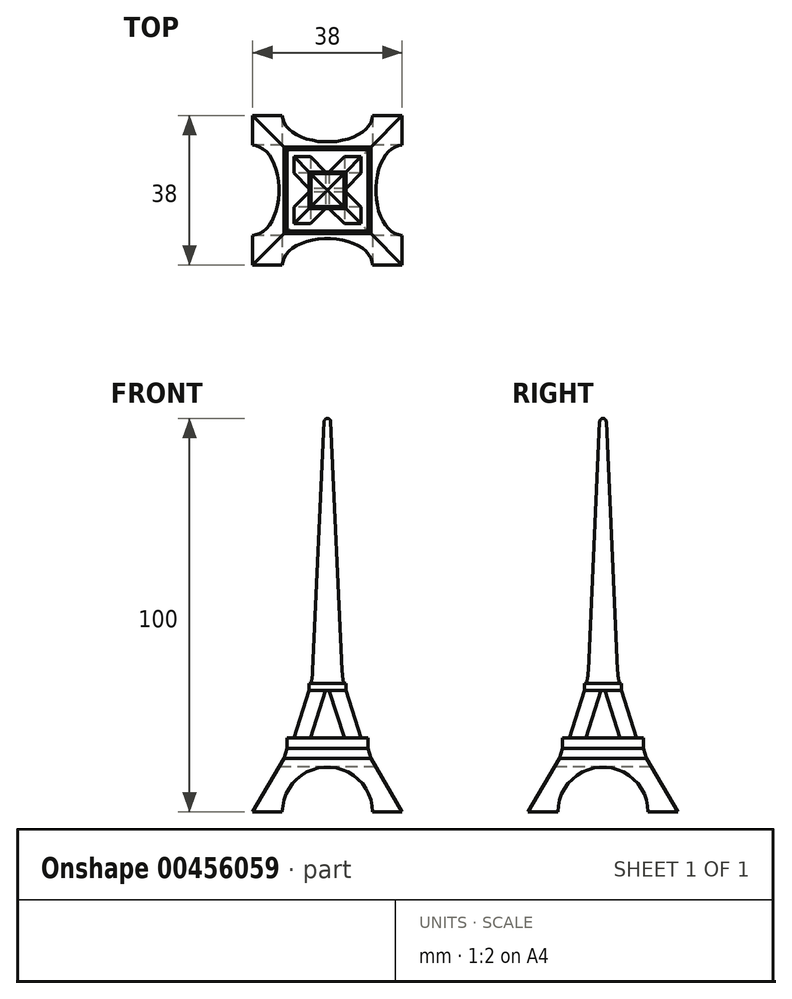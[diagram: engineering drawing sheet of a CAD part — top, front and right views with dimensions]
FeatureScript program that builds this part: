
annotation { "Feature Type Name" : "Feature", "Feature Type Description" : "" }
export const myFeature = defineFeature(function(context is Context, id is Id, definition is map)
    precondition{}
    {
        {
            var Q0;
            Q0=qCreatedBy(makeId("Front.planeOp"),FACE);
            var sketch = newSketch(context, id + "F0", { "sketchPlane" : qUnion([Q0])});
            skLineSegment(sketch, "E0.bottom", {"start": v(0, 0) * mm, "end": v(38, 0) * mm});
            skLineSegment(sketch, "E0.top", {"start": v(0, 100) * mm, "end": v(38, 100) * mm});
            skLineSegment(sketch, "E0.left", {"start": v(0, 0) * mm, "end": v(0, 100) * mm});
            skLineSegment(sketch, "E0.right", {"start": v(38, 0) * mm, "end": v(38, 100) * mm});
            skSolve(sketch);
        }
        {
            var Q0;
            Q0=makeQuery(id+"F0.imprint","IMPRINT",FACE,{"disambiguationData":[TD([[makeQuery(id+"F0.imprint","IMPRINT",EDGE,{"derivedFrom":sQuery(id+"F0.wireOp",EDGE,"E0.bottom")}),1.0]])]});
            extrude(context, id + "F1", {"entities" : qUnion([Q0]), "depth" : 38 * mm});
        }
        {
            var Q0;
            Q0=makeQuery(id+"F1.opExtrude","CAP_FACE",FACE,{"disambiguationData":[OSD([sQuery(id+"F0.wireOp",EDGE,"E0.bottom"),sQuery(id+"F0.wireOp",EDGE,"E0.top"),sQuery(id+"F0.wireOp",EDGE,"E0.left"),sQuery(id+"F0.wireOp",EDGE,"E0.right")])],"isStart":false});
            var sketch = newSketch(context, id + "F2", { "sketchPlane" : qUnion([Q0])});
            skPoint(sketch, "E1.endSnap0", {"position": v(19, 100) * mm});
            skLineSegment(sketch, "E2", {"start": v(19, 100) * mm, "end": v(19, 0) * mm, "construction": true});
            skLineSegment(sketch, "E3", {"start": v(19, 100) * mm, "end": v(19.03, 100) * mm});
            skLineSegment(sketch, "E4", {"start": v(19.83, 99.24) * mm, "end": v(22.72, 36.04) * mm});
            skLineSegment(sketch, "E5", {"start": v(38, 0) * mm, "end": v(29.32, 14.77) * mm});
            skLineSegment(sketch, "E6", {"start": v(27.53, 18.8) * mm, "end": v(23.66, 30.85) * mm});
            skArc(sketch, "E7", {"start": v(30.49, 0) * mm, "mid": v(27.12, 8.12) * mm, "end": v(19, 11.49) * mm});
            skLineSegment(sketch, "E8", {"start": v(38, 0) * mm, "end": v(30.49, 0) * mm});
            skPoint(sketch, "E9.visualSharp", {"position": v(22.85, 33.38) * mm});
            skArc(sketch, "E9.filletArc", {"start": v(22.72, 36.04) * mm, "mid": v(22.88, 34.33) * mm, "end": v(23.17, 32.64) * mm});
            skPoint(sketch, "E10.visualSharp", {"position": v(28.2, 16.68) * mm});
            skLineSegment(sketch, "E11.MirrorCS", {"start": v(18.17, 99.24) * mm, "end": v(15.28, 36.04) * mm});
            skArc(sketch, "E12.MirrorCS", {"start": v(15.28, 36.04) * mm, "mid": v(15.12, 34.33) * mm, "end": v(14.83, 32.64) * mm});
            skLineSegment(sketch, "E13.MirrorCS", {"start": v(10.47, 18.8) * mm, "end": v(14.34, 30.85) * mm});
            skLineSegment(sketch, "E14.MirrorCS", {"start": v(19, 100) * mm, "end": v(18.97, 100) * mm});
            skLineSegment(sketch, "E15.MirrorCS", {"start": v(0, 0) * mm, "end": v(8.68, 14.77) * mm});
            skArc(sketch, "E16.MirrorCS", {"start": v(7.51, 0) * mm, "mid": v(10.88, 8.12) * mm, "end": v(19, 11.49) * mm});
            skLineSegment(sketch, "E17.MirrorCS", {"start": v(0, 0) * mm, "end": v(7.51, 0) * mm});
            skLineSegment(sketch, "E18.bottom", {"start": v(-8.57, -4.89) * mm, "end": v(50.47, -4.89) * mm});
            skLineSegment(sketch, "E18.top", {"start": v(-8.57, 109.12) * mm, "end": v(50.47, 109.12) * mm});
            skLineSegment(sketch, "E18.left", {"start": v(-8.57, -4.89) * mm, "end": v(-8.57, 109.12) * mm});
            skLineSegment(sketch, "E18.right", {"start": v(50.47, -4.89) * mm, "end": v(50.47, 109.12) * mm});
            skLineSegment(sketch, "E19", {"start": v(29.32, 14.77) * mm, "end": v(29.32, 18.8) * mm});
            skLineSegment(sketch, "E20", {"start": v(29.32, 18.8) * mm, "end": v(27.53, 18.8) * mm});
            skLineSegment(sketch, "E21.MirrorCS", {"start": v(8.68, 18.8) * mm, "end": v(10.47, 18.8) * mm});
            skLineSegment(sketch, "E22.MirrorCS", {"start": v(8.68, 14.77) * mm, "end": v(8.68, 18.8) * mm});
            skLineSegment(sketch, "E23", {"start": v(23.66, 30.85) * mm, "end": v(23.66, 32.64) * mm});
            skLineSegment(sketch, "E24", {"start": v(23.66, 32.64) * mm, "end": v(23.17, 32.64) * mm});
            skLineSegment(sketch, "E25.MirrorCS", {"start": v(14.34, 30.85) * mm, "end": v(14.34, 32.64) * mm});
            skLineSegment(sketch, "E26.MirrorCS", {"start": v(14.34, 32.64) * mm, "end": v(14.83, 32.64) * mm});
            skPoint(sketch, "E27.orphan", {"position": v(14.34, 30.85) * mm});
            skPoint(sketch, "E28.visualSharp", {"position": v(18.2, 100) * mm});
            skArc(sketch, "E28.filletArc", {"start": v(18.97, 100) * mm, "mid": v(18.42, 99.78) * mm, "end": v(18.17, 99.24) * mm});
            skPoint(sketch, "E29.visualSharp", {"position": v(19.8, 100) * mm});
            skArc(sketch, "E29.filletArc", {"start": v(19.83, 99.24) * mm, "mid": v(19.58, 99.78) * mm, "end": v(19.03, 100) * mm});
            skLineSegment(sketch, "E30.0", {"start": v(14.67, 18.8) * mm, "end": v(18.54, 30.85) * mm});
            skLineSegment(sketch, "E31.0", {"start": v(23.33, 18.8) * mm, "end": v(19.46, 30.85) * mm});
            skLineSegment(sketch, "E32", {"start": v(23.33, 18.8) * mm, "end": v(14.67, 18.8) * mm});
            skLineSegment(sketch, "E33", {"start": v(19.46, 30.85) * mm, "end": v(18.54, 30.85) * mm});
            skSolve(sketch);
        }
        {
            var Q0;
            {var subQ2=sQuery(id+"F2.wireOp",EDGE,"E11.MirrorCS");Q0=makeQuery(id+"F2.imprint","IMPRINT",FACE,{"disambiguationData":[TD([[makeQuery(id+"F2.imprint","IMPRINT",EDGE,{"derivedFrom":subQ2}),-1.0]])]});}
            var Q1;
            {var subQ0=sQuery(id+"F2.wireOp",EDGE,"E7");Q1=makeQuery(id+"F2.imprint","IMPRINT",FACE,{"disambiguationData":[TD([[makeQuery(id+"F2.imprint","IMPRINT",EDGE,{"derivedFrom":subQ0}),1.0]])]});}
            var Q2;
            {var subQ2=sQuery(id+"F2.wireOp",EDGE,"E4");Q2=makeQuery(id+"F2.imprint","IMPRINT",FACE,{"disambiguationData":[TD([[makeQuery(id+"F2.imprint","IMPRINT",EDGE,{"derivedFrom":subQ2}),1.0]])]});}
            var Q3;
            Q3=makeQuery(id+"F2.imprint","IMPRINT",FACE,{"disambiguationData":[TD([[makeQuery(id+"F2.imprint","IMPRINT",EDGE,{"derivedFrom":sQuery(id+"F2.wireOp",EDGE,"E30.0")}),-1.0]])]});
            extrude(context, id + "F3", {"entities" : qUnion([Q0, Q1, Q2, Q3]), "operationType" : NewBodyOperationType.REMOVE, "endBound" : BoundingType.THROUGH_ALL, "oppositeDirection" : true, "depth" : 25 * mm});
        }
        {
            var Q0;
            Q0=qCreatedBy(makeId("Right.planeOp"),FACE);
            var sketch = newSketch(context, id + "F4", { "sketchPlane" : qUnion([Q0])});
            skPoint(sketch, "E34.endSnap0", {"position": v(-19, 100) * mm});
            skLineSegment(sketch, "E35", {"start": v(-19, 100) * mm, "end": v(-19, 0) * mm, "construction": true});
            skLineSegment(sketch, "E36", {"start": v(-19, 100) * mm, "end": v(-18.97, 100) * mm});
            skLineSegment(sketch, "E37", {"start": v(-18.17, 99.24) * mm, "end": v(-15.28, 36.04) * mm});
            skLineSegment(sketch, "E38", {"start": v(0, 0) * mm, "end": v(-8.68, 14.77) * mm});
            skLineSegment(sketch, "E39", {"start": v(-10.47, 18.8) * mm, "end": v(-14.34, 30.85) * mm});
            skArc(sketch, "E40", {"start": v(-7.51, 0) * mm, "mid": v(-10.88, 8.12) * mm, "end": v(-19, 11.49) * mm});
            skLineSegment(sketch, "E41", {"start": v(0, 0) * mm, "end": v(-7.51, 0) * mm});
            skPoint(sketch, "E42.visualSharp", {"position": v(-15.15, 33.38) * mm});
            skArc(sketch, "E42.filletArc", {"start": v(-15.28, 36.04) * mm, "mid": v(-15.12, 34.33) * mm, "end": v(-14.83, 32.64) * mm});
            skPoint(sketch, "E43.visualSharp", {"position": v(-9.8, 16.68) * mm});
            skLineSegment(sketch, "E44.MirrorCS", {"start": v(-19.83, 99.24) * mm, "end": v(-22.72, 36.04) * mm});
            skArc(sketch, "E45.MirrorCS", {"start": v(-22.72, 36.04) * mm, "mid": v(-22.88, 34.33) * mm, "end": v(-23.17, 32.64) * mm});
            skLineSegment(sketch, "E46.MirrorCS", {"start": v(-27.53, 18.8) * mm, "end": v(-23.66, 30.85) * mm});
            skLineSegment(sketch, "E47.MirrorCS", {"start": v(-19, 100) * mm, "end": v(-19.03, 100) * mm});
            skLineSegment(sketch, "E48.MirrorCS", {"start": v(-38, 0) * mm, "end": v(-29.32, 14.77) * mm});
            skArc(sketch, "E49.MirrorCS", {"start": v(-30.49, 0) * mm, "mid": v(-27.12, 8.12) * mm, "end": v(-19, 11.49) * mm});
            skLineSegment(sketch, "E50.MirrorCS", {"start": v(-38, 0) * mm, "end": v(-30.49, 0) * mm});
            skLineSegment(sketch, "E51.bottom", {"start": v(-46.57, -4.89) * mm, "end": v(12.47, -4.89) * mm});
            skLineSegment(sketch, "E51.top", {"start": v(-46.57, 109.12) * mm, "end": v(12.47, 109.12) * mm});
            skLineSegment(sketch, "E51.left", {"start": v(-46.57, -4.89) * mm, "end": v(-46.57, 109.12) * mm});
            skLineSegment(sketch, "E51.right", {"start": v(12.47, -4.89) * mm, "end": v(12.47, 109.12) * mm});
            skLineSegment(sketch, "E52", {"start": v(-8.68, 14.77) * mm, "end": v(-8.68, 18.8) * mm});
            skLineSegment(sketch, "E53", {"start": v(-8.68, 18.8) * mm, "end": v(-10.47, 18.8) * mm});
            skLineSegment(sketch, "E54.MirrorCS", {"start": v(-29.32, 18.8) * mm, "end": v(-27.53, 18.8) * mm});
            skLineSegment(sketch, "E55.MirrorCS", {"start": v(-29.32, 14.77) * mm, "end": v(-29.32, 18.8) * mm});
            skLineSegment(sketch, "E56", {"start": v(-14.34, 30.85) * mm, "end": v(-14.34, 32.64) * mm});
            skLineSegment(sketch, "E57", {"start": v(-14.34, 32.64) * mm, "end": v(-14.83, 32.64) * mm});
            skLineSegment(sketch, "E58.MirrorCS", {"start": v(-23.66, 30.85) * mm, "end": v(-23.66, 32.64) * mm});
            skLineSegment(sketch, "E59.MirrorCS", {"start": v(-23.66, 32.64) * mm, "end": v(-23.17, 32.64) * mm});
            skPoint(sketch, "E60.MirrorCS.center.orphan", {"position": v(-46.57, 24.9) * mm});
            skPoint(sketch, "E60.MirrorCS.start.orphan", {"position": v(-27.53, 18.8) * mm});
            skPoint(sketch, "E61.orphan", {"position": v(-23.66, 30.85) * mm});
            skLineSegment(sketch, "E62.0", {"start": v(-23.33, 18.8) * mm, "end": v(-19.46, 30.85) * mm});
            skLineSegment(sketch, "E63.0", {"start": v(-14.67, 18.8) * mm, "end": v(-18.54, 30.85) * mm});
            skLineSegment(sketch, "E64", {"start": v(-14.67, 18.8) * mm, "end": v(-23.33, 18.8) * mm});
            skLineSegment(sketch, "E65", {"start": v(-14.34, 30.85) * mm, "end": v(-23.66, 30.85) * mm});
            skPoint(sketch, "E66.visualSharp", {"position": v(-19.8, 100) * mm});
            skArc(sketch, "E66.filletArc", {"start": v(-19.03, 100) * mm, "mid": v(-19.58, 99.78) * mm, "end": v(-19.83, 99.24) * mm});
            skPoint(sketch, "E67.visualSharp", {"position": v(-18.2, 100) * mm});
            skArc(sketch, "E67.filletArc", {"start": v(-18.17, 99.24) * mm, "mid": v(-18.42, 99.78) * mm, "end": v(-18.97, 100) * mm});
            skSolve(sketch);
        }
        {
            var Q0;
            Q0=makeQuery(id+"F4.imprint","IMPRINT",FACE,{"disambiguationData":[TD([[makeQuery(id+"F4.imprint","IMPRINT",EDGE,{"derivedFrom":sQuery(id+"F4.wireOp",EDGE,"E36")}),1.0]])]});
            var Q1;
            Q1=makeQuery(id+"F4.imprint","IMPRINT",FACE,{"disambiguationData":[TD([[makeQuery(id+"F4.imprint","IMPRINT",EDGE,{"derivedFrom":sQuery(id+"F4.wireOp",EDGE,"E62.0")}),-1.0]])]});
            extrude(context, id + "F5", {"entities" : qUnion([Q0, Q1]), "operationType" : NewBodyOperationType.REMOVE, "endBound" : BoundingType.THROUGH_ALL, "depth" : 25 * mm});
        }
        {
            var Q0;
            Q0=makeQuery(id+"F3.boolean.opBoolean","COPY",EDGE,{"derivedFrom":makeQuery(id+"F3.opExtrude","SWEPT_EDGE",EDGE,{"disambiguationData":[OSD([sQuery(id+"F2.wireOp",EDGE,"E15.MirrorCS"),sQuery(id+"F2.wireOp",EDGE,"E22.MirrorCS")])]})});
            var Q1;
            Q1=makeQuery(id+"F5.boolean.opBoolean","COPY",EDGE,{"derivedFrom":makeQuery(id+"F5.opExtrude","SWEPT_EDGE",EDGE,{"disambiguationData":[OSD([sQuery(id+"F4.wireOp",EDGE,"E48.MirrorCS"),sQuery(id+"F4.wireOp",EDGE,"E55.MirrorCS")])]})});
            var Q2;
            Q2=makeQuery(id+"F3.boolean.opBoolean","COPY",EDGE,{"derivedFrom":makeQuery(id+"F3.opExtrude","SWEPT_EDGE",EDGE,{"disambiguationData":[OSD([sQuery(id+"F2.wireOp",EDGE,"E5"),sQuery(id+"F2.wireOp",EDGE,"E19")])]})});
            var Q3;
            Q3=makeQuery(id+"F5.boolean.opBoolean","COPY",EDGE,{"derivedFrom":makeQuery(id+"F5.opExtrude","SWEPT_EDGE",EDGE,{"disambiguationData":[OSD([sQuery(id+"F4.wireOp",EDGE,"E38"),sQuery(id+"F4.wireOp",EDGE,"E52")])]})});
            chamfer(context, id + "F6", {"entities" : qUnion([Q0, Q1, Q2, Q3]), "width" : 5 * mm, "tangentPropagation" : true});
        }
    });
